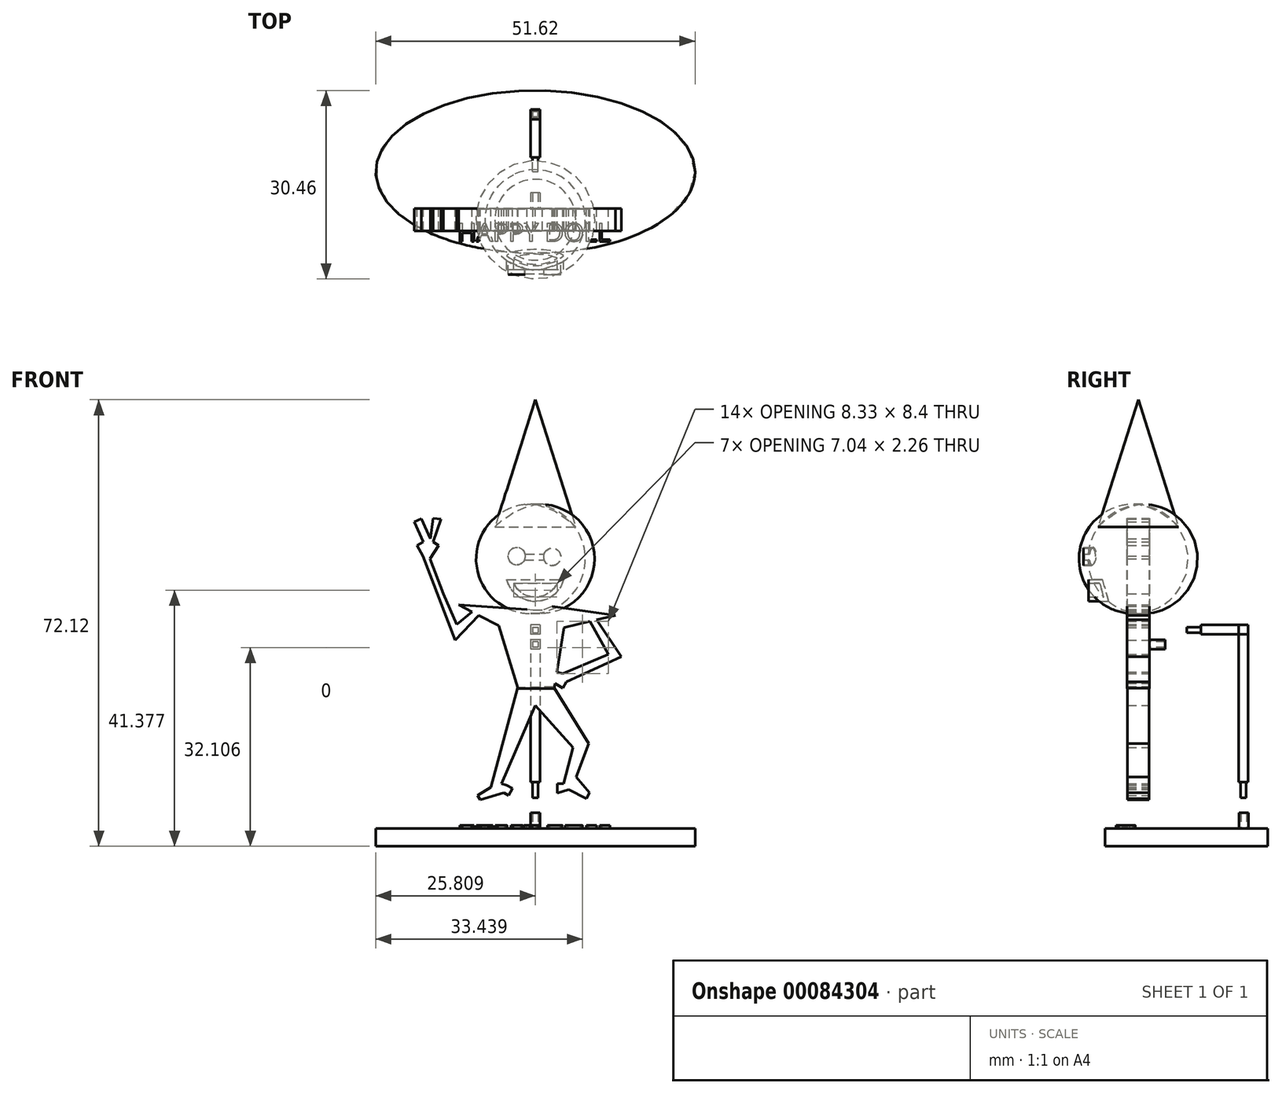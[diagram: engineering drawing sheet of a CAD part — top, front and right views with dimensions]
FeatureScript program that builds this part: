
annotation { "Feature Type Name" : "Feature", "Feature Type Description" : "" }
export const myFeature = defineFeature(function(context is Context, id is Id, definition is map)
    precondition{}
    {
        {
            var Q0;
            Q0=qCreatedBy(makeId("Front.planeOp"),FACE);
            var sketch = newSketch(context, id + "F0", { "sketchPlane" : qUnion([Q0])});
            skLineSegment(sketch, "E0", {"start": v(0, 24.17) * mm, "end": v(0, 41.76) * mm});
            skArc(sketch, "E1", {"start": v(0, 24.17) * mm, "mid": v(8.09, 32.97) * mm, "end": v(0, 41.76) * mm});
            skSolve(sketch);
        }
        {
            var Q0;
            Q0=makeQuery(id+"F0.imprint","IMPRINT",FACE,{"disambiguationData":[TD([[makeQuery(id+"F0.imprint","IMPRINT",EDGE,{"derivedFrom":sQuery(id+"F0.wireOp",EDGE,"E0")}),-1.0]])]});
            var Q1;
            Q1=sQuery(id+"F0.wireOp",EDGE,"E0");
            revolve(context, id + "F1", {"entities" : qUnion([Q0]), "axis" : qUnion([Q1]), "revolveType" : RevolveType.FULL});
        }
        {
            var Q0;
            Q0=qCreatedBy(makeId("Front.planeOp"),FACE);
            var sketch = newSketch(context, id + "F2", { "sketchPlane" : qUnion([Q0])});
            skLineSegment(sketch, "E2", {"start": v(0, 41.87) * mm, "end": v(0, 58.8) * mm});
            skLineSegment(sketch, "E3", {"start": v(0, 58.8) * mm, "end": v(6.88, 37.1) * mm});
            skFitSpline(sketch, "E4", {"points": [v(0, 41.87) * mm, v(2.83, 40.92) * mm, v(4.74, 39.73) * mm, v(6.53, 38.21) * mm, v(6.88, 37.1) * mm], "startDerivative": vector(10.25, -2.9) * mm, "endDerivative": vector(0.8, -6) * mm});
            skSolve(sketch);
        }
        {
            var Q0;
            {var subQ0=sQuery(id+"F2.wireOp",EDGE,"E2");Q0=makeQuery(id+"F2.imprint","IMPRINT",FACE,{"disambiguationData":[TD([[makeQuery(id+"F2.imprint","IMPRINT",EDGE,{"derivedFrom":subQ0}),-1.0]])]});}
            var Q1;
            Q1=sQuery(id+"F2.wireOp",EDGE,"E2");
            revolve(context, id + "F3", {"entities" : qUnion([Q0]), "axis" : qUnion([Q1]), "revolveType" : RevolveType.FULL});
        }
        {
            var Q0;
            Q0=qCreatedBy(makeId("Front.planeOp"),FACE);
            var sketch = newSketch(context, id + "F4", { "sketchPlane" : qUnion([Q0])});
            skCircle(sketch, "E5", {"center": v(2.71, 33.3) * mm, "radius": 1.4 * mm});
            skCircle(sketch, "E6", {"center": v(-3, 33.41) * mm, "radius": 1.4 * mm});
            skSolve(sketch);
        }
        {
            var Q0;
            Q0 = qSketchRegion(id + "F4", true);
            extrude(context, id + "F5", {"entities" : qUnion([Q0]), "operationType" : NewBodyOperationType.ADD, "depth" : 8.84 * mm});
        }
        {
            var Q0;
            Q0=qCreatedBy(makeId("Front.planeOp"),FACE);
            var sketch = newSketch(context, id + "F6", { "sketchPlane" : qUnion([Q0])});
            skLineSegment(sketch, "E7.bottom", {"start": v(-1.83, 33.77) * mm, "end": v(1.83, 33.77) * mm});
            skLineSegment(sketch, "E7.top", {"start": v(-1.83, 32.82) * mm, "end": v(1.83, 32.82) * mm});
            skLineSegment(sketch, "E7.left", {"start": v(-1.83, 33.77) * mm, "end": v(-1.83, 32.82) * mm});
            skLineSegment(sketch, "E7.right", {"start": v(1.83, 33.77) * mm, "end": v(1.83, 32.82) * mm});
            skPoint(sketch, "E7.middle", {"position": v(0, 33.3) * mm});
            skSolve(sketch);
        }
        {
            var Q0;
            Q0 = qSketchRegion(id + "F6", true);
            extrude(context, id + "F7", {"entities" : qUnion([Q0]), "operationType" : NewBodyOperationType.ADD, "depth" : 8.73 * mm});
        }
        {
            var Q0;
            Q0=qCreatedBy(makeId("Front.planeOp"),FACE);
            var sketch = newSketch(context, id + "F8", { "sketchPlane" : qUnion([Q0])});
            skLineSegment(sketch, "E8", {"start": v(-4.63, 29.6) * mm, "end": v(4.58, 29.6) * mm});
            skArc(sketch, "E9", {"start": v(-4.63, 29.6) * mm, "mid": v(-0.03, 26.1) * mm, "end": v(4.58, 29.6) * mm});
            skLineSegment(sketch, "E10", {"start": v(-3.52, 29.06) * mm, "end": v(3.52, 29.06) * mm});
            skArc(sketch, "E11", {"start": v(-3.52, 29.06) * mm, "mid": v(0, 26.8) * mm, "end": v(3.52, 29.06) * mm});
            skSolve(sketch);
        }
        {
            var Q0;
            Q0=makeQuery(id+"F8.imprint","IMPRINT",FACE,{"disambiguationData":[TD([[makeQuery(id+"F8.imprint","IMPRINT",EDGE,{"derivedFrom":sQuery(id+"F8.wireOp",EDGE,"E8")}),-1.0]])]});
            extrude(context, id + "F9", {"entities" : qUnion([Q0]), "operationType" : NewBodyOperationType.ADD, "depth" : 8.04 * mm});
        }
        {
            var Q0;
            Q0=qCreatedBy(makeId("Front.planeOp"),FACE);
            var sketch = newSketch(context, id + "F10", { "sketchPlane" : qUnion([Q0])});
            skLineSegment(sketch, "E12", {"start": v(-1.33, 24.4) * mm, "end": v(-12.4, 25.15) * mm});
            skLineSegment(sketch, "E13", {"start": v(-12.4, 25.15) * mm, "end": v(-5.92, 21.78) * mm});
            skLineSegment(sketch, "E14", {"start": v(-5.92, 21.78) * mm, "end": v(-2.78, 11.6) * mm});
            skLineSegment(sketch, "E15", {"start": v(-2.78, 11.6) * mm, "end": v(3.03, 11.6) * mm});
            skLineSegment(sketch, "E16", {"start": v(3.03, 11.6) * mm, "end": v(4.62, 21.5) * mm});
            skLineSegment(sketch, "E17", {"start": v(4.62, 21.5) * mm, "end": v(12.97, 23.42) * mm});
            skLineSegment(sketch, "E18", {"start": v(12.97, 23.42) * mm, "end": v(2.7, 24.87) * mm});
            skLineSegment(sketch, "E19", {"start": v(2.7, 24.87) * mm, "end": v(1.15, 24.26) * mm});
            skLineSegment(sketch, "E20", {"start": v(1.15, 24.26) * mm, "end": v(-0.4, 24.26) * mm});
            skLineSegment(sketch, "E21", {"start": v(-0.4, 24.26) * mm, "end": v(-1.33, 24.4) * mm});
            skLineSegment(sketch, "E22", {"start": v(-10.22, 24.02) * mm, "end": v(-12.72, 21.97) * mm});
            skLineSegment(sketch, "E23", {"start": v(-12.72, 21.97) * mm, "end": v(-14.88, 26.94) * mm});
            skLineSegment(sketch, "E24", {"start": v(-14.88, 26.94) * mm, "end": v(-17, 32.58) * mm});
            skLineSegment(sketch, "E25", {"start": v(-17, 32.58) * mm, "end": v(-15.6, 34.72) * mm});
            skLineSegment(sketch, "E26", {"start": v(-15.6, 34.72) * mm, "end": v(-16.5, 35.3) * mm});
            skLineSegment(sketch, "E27", {"start": v(-16.5, 35.3) * mm, "end": v(-15.28, 38.98) * mm});
            skLineSegment(sketch, "E28", {"start": v(-15.28, 38.98) * mm, "end": v(-16.5, 39.15) * mm});
            skLineSegment(sketch, "E29", {"start": v(-16.5, 39.15) * mm, "end": v(-16.95, 35.83) * mm});
            skLineSegment(sketch, "E30", {"start": v(-16.95, 35.83) * mm, "end": v(-18.4, 39.06) * mm});
            skLineSegment(sketch, "E31", {"start": v(-18.4, 39.06) * mm, "end": v(-19.54, 38.55) * mm});
            skLineSegment(sketch, "E32", {"start": v(-19.54, 38.55) * mm, "end": v(-18.09, 35.3) * mm});
            skLineSegment(sketch, "E33", {"start": v(-18.09, 35.3) * mm, "end": v(-19.13, 34.72) * mm});
            skLineSegment(sketch, "E34", {"start": v(-19.13, 34.72) * mm, "end": v(-18.19, 33.03) * mm});
            skLineSegment(sketch, "E35", {"start": v(-18.19, 33.03) * mm, "end": v(-12.98, 19.46) * mm});
            skLineSegment(sketch, "E36", {"start": v(-12.98, 19.46) * mm, "end": v(-9.16, 23.47) * mm});
            skLineSegment(sketch, "E37", {"start": v(9.91, 22.72) * mm, "end": v(13.93, 16.75) * mm});
            skLineSegment(sketch, "E38", {"start": v(13.93, 16.75) * mm, "end": v(4.99, 12.73) * mm});
            skLineSegment(sketch, "E39", {"start": v(4.99, 12.73) * mm, "end": v(4.41, 11.67) * mm});
            skLineSegment(sketch, "E40", {"start": v(4.41, 11.67) * mm, "end": v(3.02, 12.57) * mm});
            skLineSegment(sketch, "E41", {"start": v(3.02, 12.57) * mm, "end": v(3.46, 14.31) * mm});
            skLineSegment(sketch, "E42", {"start": v(3.46, 14.31) * mm, "end": v(4.43, 14.06) * mm});
            skLineSegment(sketch, "E43", {"start": v(11.8, 17.16) * mm, "end": v(4.43, 14.06) * mm});
            skLineSegment(sketch, "E44", {"start": v(11.8, 17.16) * mm, "end": v(8.8, 22.46) * mm});
            skSolve(sketch);
        }
        {
            var Q0;
            Q0 = qSketchRegion(id + "F10", true);
            extrude(context, id + "F11", {"entities" : qUnion([Q0]), "endBound" : BoundingType.SYMMETRIC, "depth" : 3.58 * mm});
        }
        {
            var Q0;
            Q0=qCreatedBy(makeId("Front.planeOp"),FACE);
            var sketch = newSketch(context, id + "F12", { "sketchPlane" : qUnion([Q0])});
            skLineSegment(sketch, "E45", {"start": v(-2.86, 11.47) * mm, "end": v(-7.18, -4.63) * mm});
            skLineSegment(sketch, "E46", {"start": v(-7.18, -4.63) * mm, "end": v(-9.35, -5.9) * mm});
            skLineSegment(sketch, "E47", {"start": v(-9.35, -5.9) * mm, "end": v(-8.93, -6.62) * mm});
            skLineSegment(sketch, "E48", {"start": v(-8.93, -6.62) * mm, "end": v(-5.08, -5.46) * mm});
            skLineSegment(sketch, "E49", {"start": v(-5.08, -5.46) * mm, "end": v(-4.3, -5.9) * mm});
            skLineSegment(sketch, "E50", {"start": v(-4.3, -5.9) * mm, "end": v(-3.68, -4.81) * mm});
            skLineSegment(sketch, "E51", {"start": v(-3.68, -4.81) * mm, "end": v(-4.62, -4.28) * mm});
            skLineSegment(sketch, "E52", {"start": v(-4.62, -4.28) * mm, "end": v(-5.43, -4.06) * mm});
            skLineSegment(sketch, "E53", {"start": v(-5.43, -4.06) * mm, "end": v(0, 8.64) * mm});
            skLineSegment(sketch, "E54", {"start": v(0, 8.64) * mm, "end": v(6.08, 1.81) * mm});
            skLineSegment(sketch, "E55", {"start": v(6.08, 1.81) * mm, "end": v(4.58, -4.02) * mm});
            skLineSegment(sketch, "E56", {"start": v(4.58, -4.02) * mm, "end": v(3.53, -4.02) * mm});
            skLineSegment(sketch, "E57", {"start": v(3.53, -4.02) * mm, "end": v(3.53, -5.57) * mm});
            skLineSegment(sketch, "E58", {"start": v(3.53, -5.57) * mm, "end": v(5.41, -4.96) * mm});
            skLineSegment(sketch, "E59", {"start": v(5.41, -4.96) * mm, "end": v(8.24, -6.46) * mm});
            skLineSegment(sketch, "E60", {"start": v(8.24, -6.46) * mm, "end": v(8.75, -5.51) * mm});
            skLineSegment(sketch, "E61", {"start": v(8.75, -5.51) * mm, "end": v(6.58, -2.96) * mm});
            skLineSegment(sketch, "E62", {"start": v(6.58, -2.96) * mm, "end": v(8.63, 2.48) * mm});
            skLineSegment(sketch, "E63", {"start": v(8.63, 2.48) * mm, "end": v(2.97, 11.64) * mm});
            skLineSegment(sketch, "E64", {"start": v(2.97, 11.64) * mm, "end": v(-2.86, 11.47) * mm});
            skSolve(sketch);
        }
        {
            var Q0;
            Q0 = qSketchRegion(id + "F12", true);
            extrude(context, id + "F13", {"entities" : qUnion([Q0]), "endBound" : BoundingType.SYMMETRIC, "depth" : 3.53 * mm});
        }
        {
            var Q0;
            Q0=makeQuery(id+"F13.opExtrude","SWEPT_BODY",BODY,{"disambiguationData":[OSD([sQuery(id+"F12.wireOp",EDGE,"E45"),sQuery(id+"F12.wireOp",EDGE,"E46"),sQuery(id+"F12.wireOp",EDGE,"E47"),sQuery(id+"F12.wireOp",EDGE,"E48"),sQuery(id+"F12.wireOp",EDGE,"E49"),sQuery(id+"F12.wireOp",EDGE,"E50"),sQuery(id+"F12.wireOp",EDGE,"E51"),sQuery(id+"F12.wireOp",EDGE,"E52"),sQuery(id+"F12.wireOp",EDGE,"E53"),sQuery(id+"F12.wireOp",EDGE,"E54"),sQuery(id+"F12.wireOp",EDGE,"E55"),sQuery(id+"F12.wireOp",EDGE,"E56"),sQuery(id+"F12.wireOp",EDGE,"E57"),sQuery(id+"F12.wireOp",EDGE,"E58"),sQuery(id+"F12.wireOp",EDGE,"E59"),sQuery(id+"F12.wireOp",EDGE,"E60"),sQuery(id+"F12.wireOp",EDGE,"E61"),sQuery(id+"F12.wireOp",EDGE,"E62"),sQuery(id+"F12.wireOp",EDGE,"E63"),sQuery(id+"F12.wireOp",EDGE,"E64")])]});
            transform(context, id + "F14", {"entities" : qUnion([Q0]), "transformType" : TransformType.TRANSLATION_3D, "dx" : 0 * mm, "dy" : 0 * mm, "dz" : 0.29 * mm, "makeCopy" : false});
        }
        {
            var Q0;
            Q0=makeQuery(id+"F1.opRevolve","SWEPT_BODY",BODY,{"disambiguationData":[OSD([sQuery(id+"F0.wireOp",EDGE,"E0"),sQuery(id+"F0.wireOp",EDGE,"E1")])]});
            transform(context, id + "F15", {"entities" : qUnion([Q0]), "transformType" : TransformType.TRANSLATION_3D, "dx" : 0 * mm, "dy" : 0 * mm, "dz" : -0.4 * mm, "makeCopy" : false});
        }
        {
            var Q0;
            Q0=makeQuery(id+"F3.opRevolve","SWEPT_BODY",BODY,{"disambiguationData":[OSD([sQuery(id+"F2.wireOp",EDGE,"E3"),sQuery(id+"F2.wireOp",EDGE,"E4"),sQuery(id+"F2.wireOp",EDGE,"E2")])]});
            transform(context, id + "F16", {"entities" : qUnion([Q0]), "transformType" : TransformType.TRANSLATION_3D, "dx" : 0 * mm, "dy" : 0 * mm, "dz" : -0.51 * mm, "makeCopy" : false});
        }
        {
            var Q0;
            Q0=qCreatedBy(makeId("Front.planeOp"),FACE);
            var sketch = newSketch(context, id + "F17", { "sketchPlane" : qUnion([Q0])});
            skLineSegment(sketch, "E65.bottom", {"start": v(0.76, 13.67) * mm, "end": v(-0.76, 13.67) * mm});
            skLineSegment(sketch, "E65.top", {"start": v(0.76, 12.15) * mm, "end": v(-0.76, 12.15) * mm});
            skLineSegment(sketch, "E65.left", {"start": v(0.76, 13.67) * mm, "end": v(0.76, 12.15) * mm});
            skLineSegment(sketch, "E65.right", {"start": v(-0.76, 13.67) * mm, "end": v(-0.76, 12.15) * mm});
            skPoint(sketch, "E65.middle", {"position": v(0, 12.91) * mm});
            skLineSegment(sketch, "E66.bottom", {"start": v(0.44, 13.36) * mm, "end": v(-0.44, 13.36) * mm});
            skLineSegment(sketch, "E66.top", {"start": v(0.44, 12.47) * mm, "end": v(-0.44, 12.47) * mm});
            skLineSegment(sketch, "E66.left", {"start": v(0.44, 13.36) * mm, "end": v(0.44, 12.47) * mm});
            skLineSegment(sketch, "E66.right", {"start": v(-0.44, 13.36) * mm, "end": v(-0.44, 12.47) * mm});
            skSolve(sketch);
        }
        {
            var Q0;
            Q0 = qSketchRegion(id + "F17", true);
            extrude(context, id + "F18", {"entities" : qUnion([Q0]), "oppositeDirection" : true, "depth" : 2.54 * mm});
        }
        {
            var Q0;
            Q0=makeQuery(id+"F18.opExtrude","SWEPT_BODY",BODY,{"disambiguationData":[OSD([sQuery(id+"F17.wireOp",EDGE,"E65.bottom"),sQuery(id+"F17.wireOp",EDGE,"E65.top"),sQuery(id+"F17.wireOp",EDGE,"E65.left"),sQuery(id+"F17.wireOp",EDGE,"E65.right"),sQuery(id+"F17.wireOp",EDGE,"E66.bottom"),sQuery(id+"F17.wireOp",EDGE,"E66.top"),sQuery(id+"F17.wireOp",EDGE,"E66.left"),sQuery(id+"F17.wireOp",EDGE,"E66.right")])]});
            transform(context, id + "F19", {"entities" : qUnion([Q0]), "transformType" : TransformType.TRANSLATION_3D, "dx" : 0 * mm, "dy" : 0 * mm, "dz" : 7.06 * mm, "makeCopy" : false});
        }
        {
            var Q0;
            Q0=qCreatedBy(makeId("Top.planeOp"),FACE);
            var sketch = newSketch(context, id + "F20", { "sketchPlane" : qUnion([Q0])});
            skEllipse(sketch, "E67", {"center": v(0, 28.63) * mm, "majorRadius": 25.8 * mm, "minorRadius": 13.14 * mm, "majorAxis": v(1, 0)});
            skSolve(sketch);
        }
        {
            var Q0;
            Q0 = qSketchRegion(id + "F20", true);
            extrude(context, id + "F21", {"entities" : qUnion([Q0]), "depth" : 2.88 * mm});
        }
        {
            var Q0;
            Q0=makeQuery(id+"F21.opExtrude","SWEPT_BODY",BODY,{"disambiguationData":[OSD([sQuery(id+"F20.wireOp",EDGE,"E67")])]});
            transform(context, id + "F22", {"entities" : qUnion([Q0]), "transformType" : TransformType.TRANSLATION_3D, "dx" : 0 * mm, "dy" : 0 * mm, "dz" : -20.18 * mm, "makeCopy" : false});
        }
        {
            var Q0;
            Q0=makeQuery(id+"F21.opExtrude","CAP_FACE",FACE,{"disambiguationData":[OSD([sQuery(id+"F20.wireOp",EDGE,"E67")])],"isStart":false});
            var sketch = newSketch(context, id + "F23", { "sketchPlane" : qUnion([Q0])});
            skLineSegment(sketch, "E68.bottom", {"start": v(0.76, 38.71) * mm, "end": v(-0.76, 38.71) * mm});
            skLineSegment(sketch, "E68.top", {"start": v(0.76, 37.19) * mm, "end": v(-0.76, 37.19) * mm});
            skLineSegment(sketch, "E68.left", {"start": v(0.76, 38.71) * mm, "end": v(0.76, 37.19) * mm});
            skLineSegment(sketch, "E68.right", {"start": v(-0.76, 38.71) * mm, "end": v(-0.76, 37.19) * mm});
            skPoint(sketch, "E68.middle", {"position": v(0, 37.95) * mm});
            skPoint(sketch, "E68.middle.positionSnap0", {"position": v(0, 41.77) * mm});
            skPoint(sketch, "E68.centerSnap0", {"position": v(0, 41.77) * mm});
            skLineSegment(sketch, "E69.bottom", {"start": v(0.44, 38.4) * mm, "end": v(-0.44, 38.4) * mm});
            skLineSegment(sketch, "E69.top", {"start": v(0.44, 37.5) * mm, "end": v(-0.44, 37.5) * mm});
            skLineSegment(sketch, "E69.left", {"start": v(0.44, 38.4) * mm, "end": v(0.44, 37.5) * mm});
            skLineSegment(sketch, "E69.right", {"start": v(-0.44, 38.4) * mm, "end": v(-0.44, 37.5) * mm});
            skSolve(sketch);
        }
        {
            var Q0;
            Q0 = qSketchRegion(id + "F23", true);
            extrude(context, id + "F24", {"entities" : qUnion([Q0]), "depth" : 2.54 * mm});
        }
        {
            var Q0;
            Q0=qCreatedBy(makeId("Top.planeOp"),FACE);
            var sketch = newSketch(context, id + "F25", { "sketchPlane" : qUnion([Q0])});
            skLineSegment(sketch, "E70.bottom", {"start": v(0.76, 23.42) * mm, "end": v(-0.76, 23.42) * mm});
            skLineSegment(sketch, "E70.top", {"start": v(0.76, 21.9) * mm, "end": v(-0.76, 21.9) * mm});
            skLineSegment(sketch, "E70.left", {"start": v(0.76, 23.42) * mm, "end": v(0.76, 21.9) * mm});
            skLineSegment(sketch, "E70.right", {"start": v(-0.76, 23.42) * mm, "end": v(-0.76, 21.9) * mm});
            skPoint(sketch, "E70.middle", {"position": v(0, 22.65) * mm});
            skSolve(sketch);
        }
        {
            var Q0;
            Q0 = qSketchRegion(id + "F25", true);
            extrude(context, id + "F26", {"entities" : qUnion([Q0]), "depth" : 25.4 * mm});
        }
        {
            var Q0;
            Q0=makeQuery(id+"F26.opExtrude","SWEPT_BODY",BODY,{"disambiguationData":[OSD([sQuery(id+"F25.wireOp",EDGE,"E70.bottom"),sQuery(id+"F25.wireOp",EDGE,"E70.top"),sQuery(id+"F25.wireOp",EDGE,"E70.left"),sQuery(id+"F25.wireOp",EDGE,"E70.right")])]});
            transform(context, id + "F27", {"entities" : qUnion([Q0]), "transformType" : TransformType.TRANSLATION_3D, "dx" : 0 * mm, "dy" : 15.2 * mm, "dz" : -9.83 * mm, "makeCopy" : false});
        }
        {
            var Q0;
            Q0=makeQuery(id+"F26.opExtrude","CAP_FACE",FACE,{"disambiguationData":[OSD([sQuery(id+"F25.wireOp",EDGE,"E70.bottom"),sQuery(id+"F25.wireOp",EDGE,"E70.top"),sQuery(id+"F25.wireOp",EDGE,"E70.left"),sQuery(id+"F25.wireOp",EDGE,"E70.right")])],"isStart":true});
            var sketch = newSketch(context, id + "F28", { "sketchPlane" : qUnion([Q0])});
            skLineSegment(sketch, "E71.bottom", {"start": v(0.44, -32.2) * mm, "end": v(-0.44, -32.2) * mm});
            skLineSegment(sketch, "E71.top", {"start": v(0.44, -33.1) * mm, "end": v(-0.44, -33.1) * mm});
            skLineSegment(sketch, "E71.left", {"start": v(0.44, -32.2) * mm, "end": v(0.44, -33.1) * mm});
            skLineSegment(sketch, "E71.right", {"start": v(-0.44, -32.2) * mm, "end": v(-0.44, -33.1) * mm});
            skPoint(sketch, "E71.middle", {"position": v(0, -32.65) * mm});
            skSolve(sketch);
        }
        {
            var Q0;
            Q0 = qSketchRegion(id + "F28", true);
            extrude(context, id + "F29", {"entities" : qUnion([Q0]), "depth" : 2.54 * mm});
        }
        {
            var Q0;
            Q0=makeQuery(id+"F29.opExtrude","SWEPT_BODY",BODY,{"disambiguationData":[OSD([sQuery(id+"F28.wireOp",EDGE,"E71.bottom"),sQuery(id+"F28.wireOp",EDGE,"E71.top"),sQuery(id+"F28.wireOp",EDGE,"E71.left"),sQuery(id+"F28.wireOp",EDGE,"E71.right")])]});
            transform(context, id + "F30", {"entities" : qUnion([Q0]), "transformType" : TransformType.TRANSLATION_3D, "dx" : 0 * mm, "dy" : 5.23 * mm, "dz" : 0 * mm, "makeCopy" : false});
        }
        {
            var Q0;
            Q0=makeQuery(id+"F18.opExtrude","CAP_FACE",FACE,{"disambiguationData":[OSD([sQuery(id+"F17.wireOp",EDGE,"E65.bottom"),sQuery(id+"F17.wireOp",EDGE,"E65.top"),sQuery(id+"F17.wireOp",EDGE,"E65.left"),sQuery(id+"F17.wireOp",EDGE,"E65.right"),sQuery(id+"F17.wireOp",EDGE,"E66.bottom"),sQuery(id+"F17.wireOp",EDGE,"E66.top"),sQuery(id+"F17.wireOp",EDGE,"E66.left"),sQuery(id+"F17.wireOp",EDGE,"E66.right")])],"isStart":false});
            var sketch = newSketch(context, id + "F31", { "sketchPlane" : qUnion([Q0])});
            skLineSegment(sketch, "E72.bottom", {"start": v(-0.76, 27.91) * mm, "end": v(0.76, 27.91) * mm});
            skLineSegment(sketch, "E72.top", {"start": v(-0.76, 26.4) * mm, "end": v(0.76, 26.4) * mm});
            skLineSegment(sketch, "E72.left", {"start": v(-0.76, 27.91) * mm, "end": v(-0.76, 26.4) * mm});
            skLineSegment(sketch, "E72.right", {"start": v(0.76, 27.91) * mm, "end": v(0.76, 26.4) * mm});
            skPoint(sketch, "E72.middle", {"position": v(0, 27.15) * mm});
            skSolve(sketch);
        }
        {
            var Q0;
            Q0 = qSketchRegion(id + "F31", true);
            extrude(context, id + "F32", {"entities" : qUnion([Q0]), "depth" : 7.62 * mm});
        }
        {
            var Q0;
            Q0=makeQuery(id+"F32.opExtrude","SWEPT_BODY",BODY,{"disambiguationData":[OSD([sQuery(id+"F31.wireOp",EDGE,"E72.bottom"),sQuery(id+"F31.wireOp",EDGE,"E72.top"),sQuery(id+"F31.wireOp",EDGE,"E72.left"),sQuery(id+"F31.wireOp",EDGE,"E72.right")])]});
            transform(context, id + "F33", {"entities" : qUnion([Q0]), "transformType" : TransformType.TRANSLATION_3D, "dx" : 0 * mm, "dy" : 28.43 * mm, "dz" : -12.36 * mm, "makeCopy" : false});
        }
        {
            var Q0;
            Q0=makeQuery(id+"F32.opExtrude","CAP_FACE",FACE,{"disambiguationData":[OSD([sQuery(id+"F31.wireOp",EDGE,"E72.bottom"),sQuery(id+"F31.wireOp",EDGE,"E72.top"),sQuery(id+"F31.wireOp",EDGE,"E72.left"),sQuery(id+"F31.wireOp",EDGE,"E72.right")])],"isStart":true});
            var sketch = newSketch(context, id + "F34", { "sketchPlane" : qUnion([Q0])});
            skLineSegment(sketch, "E73.bottom", {"start": v(-0.44, 26.66) * mm, "end": v(0.44, 26.66) * mm});
            skLineSegment(sketch, "E73.top", {"start": v(-0.44, 25.77) * mm, "end": v(0.44, 25.77) * mm});
            skLineSegment(sketch, "E73.left", {"start": v(-0.44, 26.66) * mm, "end": v(-0.44, 25.77) * mm});
            skLineSegment(sketch, "E73.right", {"start": v(0.44, 26.66) * mm, "end": v(0.44, 25.77) * mm});
            skPoint(sketch, "E73.middle", {"position": v(0, 26.21) * mm});
            skPoint(sketch, "E73.middle.positionSnap0", {"position": v(0, 15.56) * mm});
            skPoint(sketch, "E73.centerSnap0", {"position": v(0, 15.56) * mm});
            skSolve(sketch);
        }
        {
            var Q0;
            Q0 = qSketchRegion(id + "F34", true);
            extrude(context, id + "F35", {"entities" : qUnion([Q0]), "depth" : 2.3 * mm});
        }
        {
            var Q0;
            Q0=makeQuery(id+"F1.opRevolve","SWEPT_BODY",BODY,{"disambiguationData":[OSD([sQuery(id+"F0.wireOp",EDGE,"E0"),sQuery(id+"F0.wireOp",EDGE,"E1")])]});
            var Q1;
            Q1=makeQuery(id+"F3.opRevolve","SWEPT_BODY",BODY,{"disambiguationData":[OSD([sQuery(id+"F2.wireOp",EDGE,"E3"),sQuery(id+"F2.wireOp",EDGE,"E4"),sQuery(id+"F2.wireOp",EDGE,"E2")])]});
            var Q2;
            Q2=qCreatedBy(id+"Fu2rmcZubVb088R_2.opHelix",BODY);
            var Q3;
            Q3=makeQuery(id+"F11.opExtrude","SWEPT_BODY",BODY,{"disambiguationData":[OSD([sQuery(id+"F10.wireOp",EDGE,"E12"),sQuery(id+"F10.wireOp",EDGE,"E13"),sQuery(id+"F10.wireOp",EDGE,"E14"),sQuery(id+"F10.wireOp",EDGE,"E15"),sQuery(id+"F10.wireOp",EDGE,"E16"),sQuery(id+"F10.wireOp",EDGE,"E17"),sQuery(id+"F10.wireOp",EDGE,"E18"),sQuery(id+"F10.wireOp",EDGE,"E19"),sQuery(id+"F10.wireOp",EDGE,"E20"),sQuery(id+"F10.wireOp",EDGE,"E21"),sQuery(id+"F10.wireOp",EDGE,"E22"),sQuery(id+"F10.wireOp",EDGE,"E23"),sQuery(id+"F10.wireOp",EDGE,"E24"),sQuery(id+"F10.wireOp",EDGE,"E25"),sQuery(id+"F10.wireOp",EDGE,"E26"),sQuery(id+"F10.wireOp",EDGE,"E27"),sQuery(id+"F10.wireOp",EDGE,"E28"),sQuery(id+"F10.wireOp",EDGE,"E29"),sQuery(id+"F10.wireOp",EDGE,"E30"),sQuery(id+"F10.wireOp",EDGE,"E31"),sQuery(id+"F10.wireOp",EDGE,"E32"),sQuery(id+"F10.wireOp",EDGE,"E33"),sQuery(id+"F10.wireOp",EDGE,"E34"),sQuery(id+"F10.wireOp",EDGE,"E35"),sQuery(id+"F10.wireOp",EDGE,"E36"),sQuery(id+"F10.wireOp",EDGE,"E37"),sQuery(id+"F10.wireOp",EDGE,"E38"),sQuery(id+"F10.wireOp",EDGE,"E39"),sQuery(id+"F10.wireOp",EDGE,"E40"),sQuery(id+"F10.wireOp",EDGE,"E42"),sQuery(id+"F10.wireOp",EDGE,"E43"),sQuery(id+"F10.wireOp",EDGE,"E44")])]});
            var Q4;
            Q4=makeQuery(id+"F13.opExtrude","SWEPT_BODY",BODY,{"disambiguationData":[OSD([sQuery(id+"F12.wireOp",EDGE,"E45"),sQuery(id+"F12.wireOp",EDGE,"E46"),sQuery(id+"F12.wireOp",EDGE,"E47"),sQuery(id+"F12.wireOp",EDGE,"E48"),sQuery(id+"F12.wireOp",EDGE,"E49"),sQuery(id+"F12.wireOp",EDGE,"E50"),sQuery(id+"F12.wireOp",EDGE,"E51"),sQuery(id+"F12.wireOp",EDGE,"E52"),sQuery(id+"F12.wireOp",EDGE,"E53"),sQuery(id+"F12.wireOp",EDGE,"E54"),sQuery(id+"F12.wireOp",EDGE,"E55"),sQuery(id+"F12.wireOp",EDGE,"E56"),sQuery(id+"F12.wireOp",EDGE,"E57"),sQuery(id+"F12.wireOp",EDGE,"E58"),sQuery(id+"F12.wireOp",EDGE,"E59"),sQuery(id+"F12.wireOp",EDGE,"E60"),sQuery(id+"F12.wireOp",EDGE,"E61"),sQuery(id+"F12.wireOp",EDGE,"E62"),sQuery(id+"F12.wireOp",EDGE,"E63"),sQuery(id+"F12.wireOp",EDGE,"E64")])]});
            var Q5;
            Q5=makeQuery(id+"F18.opExtrude","SWEPT_BODY",BODY,{"disambiguationData":[OSD([sQuery(id+"F17.wireOp",EDGE,"E65.bottom"),sQuery(id+"F17.wireOp",EDGE,"E65.top"),sQuery(id+"F17.wireOp",EDGE,"E65.left"),sQuery(id+"F17.wireOp",EDGE,"E65.right"),sQuery(id+"F17.wireOp",EDGE,"E66.bottom"),sQuery(id+"F17.wireOp",EDGE,"E66.top"),sQuery(id+"F17.wireOp",EDGE,"E66.left"),sQuery(id+"F17.wireOp",EDGE,"E66.right")])]});
            transform(context, id + "F36", {"entities" : qUnion([Q0, Q1, Q2, Q3, Q4, Q5]), "transformType" : TransformType.TRANSLATION_3D, "dx" : 0 * mm, "dy" : 20.88 * mm, "dz" : -6.34 * mm, "makeCopy" : false});
        }
        {
            var Q0;
            Q0=makeQuery(id+"F35.opExtrude","SWEPT_BODY",BODY,{"disambiguationData":[OSD([sQuery(id+"F34.wireOp",EDGE,"E73.bottom"),sQuery(id+"F34.wireOp",EDGE,"E73.top"),sQuery(id+"F34.wireOp",EDGE,"E73.left"),sQuery(id+"F34.wireOp",EDGE,"E73.right")])]});
            transform(context, id + "F37", {"entities" : qUnion([Q0]), "transformType" : TransformType.TRANSLATION_3D, "dx" : 0 * mm, "dy" : 0 * mm, "dz" : -11.43 * mm, "makeCopy" : false});
        }
        {
            var Q0;
            Q0=makeQuery(id+"F18.opExtrude","SWEPT_BODY",BODY,{"disambiguationData":[OSD([sQuery(id+"F17.wireOp",EDGE,"E65.bottom"),sQuery(id+"F17.wireOp",EDGE,"E65.top"),sQuery(id+"F17.wireOp",EDGE,"E65.left"),sQuery(id+"F17.wireOp",EDGE,"E65.right"),sQuery(id+"F17.wireOp",EDGE,"E66.bottom"),sQuery(id+"F17.wireOp",EDGE,"E66.top"),sQuery(id+"F17.wireOp",EDGE,"E66.left"),sQuery(id+"F17.wireOp",EDGE,"E66.right")])]});
            transform(context, id + "F38", {"entities" : qUnion([Q0]), "transformType" : TransformType.TRANSLATION_3D, "dx" : 0 * mm, "dy" : 1.83 * mm, "dz" : 0 * mm, "makeCopy" : false});
        }
        {
            var Q0;
            Q0=makeQuery(id+"F18.opExtrude","SWEPT_BODY",BODY,{"disambiguationData":[OSD([sQuery(id+"F17.wireOp",EDGE,"E65.bottom"),sQuery(id+"F17.wireOp",EDGE,"E65.top"),sQuery(id+"F17.wireOp",EDGE,"E65.left"),sQuery(id+"F17.wireOp",EDGE,"E65.right"),sQuery(id+"F17.wireOp",EDGE,"E66.bottom"),sQuery(id+"F17.wireOp",EDGE,"E66.top"),sQuery(id+"F17.wireOp",EDGE,"E66.left"),sQuery(id+"F17.wireOp",EDGE,"E66.right")])]});
            transform(context, id + "F39", {"entities" : qUnion([Q0]), "transformType" : TransformType.TRANSLATION_3D, "dx" : 0 * mm, "dy" : 0 * mm, "dz" : -1.22 * mm, "makeCopy" : false});
        }
        {
            var Q0;
            Q0=makeQuery(id+"F21.opExtrude","CAP_FACE",FACE,{"disambiguationData":[OSD([sQuery(id+"F20.wireOp",EDGE,"E67")])],"isStart":false});
            var sketch = newSketch(context, id + "F40", { "sketchPlane" : qUnion([Q0])});
            skText(sketch, "E74", { "text": "HAPPY DOLL", "fontName": "OpenSans-Regular.ttf"});
            const initialGuessF40  = {"E74": [-0.01259, 0.01736, 1, 0, 0.003]};
            skSetInitialGuess(sketch, initialGuessF40);
            skSolve(sketch);
        }
        {
            var Q0;
            Q0 = qSketchRegion(id + "F40", true);
            extrude(context, id + "F41", {"entities" : qUnion([Q0]), "operationType" : NewBodyOperationType.ADD, "depth" : 0.53 * mm});
        }
    });
